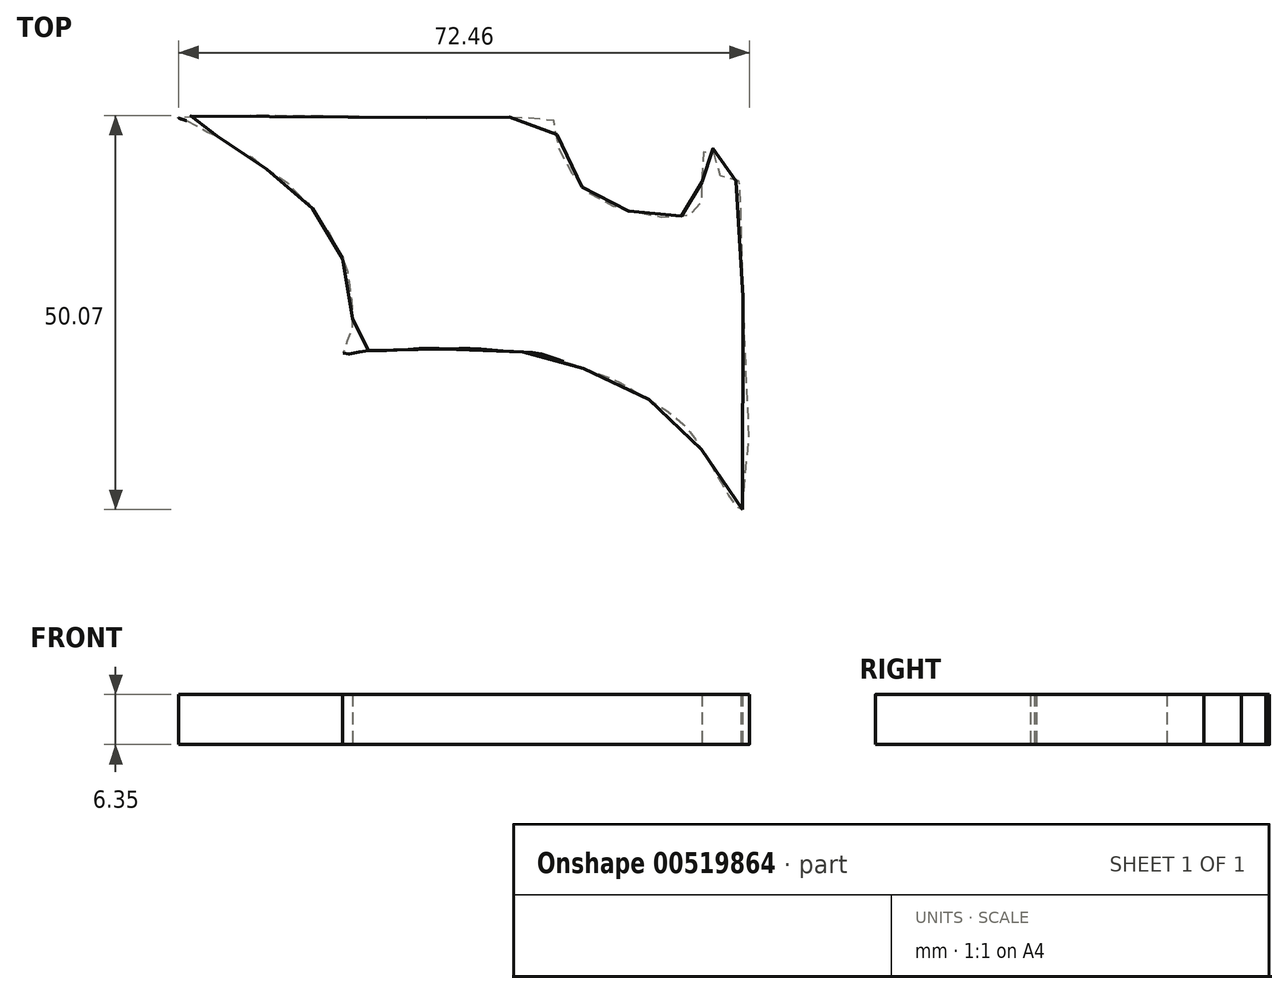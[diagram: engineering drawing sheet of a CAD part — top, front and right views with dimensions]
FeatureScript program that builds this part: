
annotation { "Feature Type Name" : "Feature", "Feature Type Description" : "" }
export const myFeature = defineFeature(function(context is Context, id is Id, definition is map)
    precondition{}
    {
        {
            var Q0;
            Q0=qCreatedBy(makeId("Top.planeOp"),FACE);
            var sketch = newSketch(context, id + "F0", { "sketchPlane" : qUnion([Q0])});
            skFitSpline(sketch, "E0", {"points": [v(0, -28.97) * mm, v(0, 0) * mm, v(0, 12.47) * mm, v(0, 12.69) * mm, v(-1.53, 12.69) * mm, v(-2.51, 12.8) * mm, v(-2.84, 13.67) * mm, v(-3.39, 15.2) * mm, v(-3.72, 16.74) * mm, v(-4.27, 17.5) * mm, v(-4.92, 16.41) * mm, v(-5.14, 14.88) * mm, v(-5.14, 13.45) * mm, v(-5.14, 11.48) * mm, v(-5.25, 9.95) * mm, v(-5.58, 9.29) * mm, v(-6.24, 8.52) * mm, v(-7.88, 8.3) * mm, v(-10.08, 8.08) * mm, v(-11.94, 8.3) * mm, v(-13.25, 8.74) * mm, v(-14.9, 8.96) * mm, v(-16.43, 9.5) * mm, v(-18.3, 10.38) * mm, v(-19.83, 11.48) * mm, v(-20.82, 12.58) * mm, v(-22.24, 14.66) * mm, v(-23.23, 16.63) * mm, v(-23.56, 18.71) * mm, v(-24, 20.47) * mm, v(-25.2, 20.58) * mm, v(-28.05, 20.8) * mm, v(-31.45, 20.8) * mm, v(-35.95, 20.8) * mm, v(-41.65, 20.8) * mm, v(-71.57, 20.8) * mm, v(-70.47, 20.36) * mm, v(-69.27, 19.7) * mm, v(-67.4, 18.71) * mm, v(-65.65, 17.95) * mm, v(-64, 16.63) * mm, v(-62.25, 15.76) * mm, v(-59.95, 13.9) * mm, v(-57.98, 12.69) * mm, v(-56.22, 10.82) * mm, v(-54.69, 9.4) * mm, v(-53.7, 7.53) * mm, v(-52.6, 6.33) * mm, v(-51.51, 4.14) * mm, v(-50.41, 2.05) * mm, v(-49.98, 0) * mm, v(-49.65, -2.55) * mm, v(-49.54, -5.07) * mm, v(-49.87, -6.94) * mm, v(-50.74, -9.13) * mm, v(-48.11, -8.9) * mm, v(-45.37, -8.8) * mm, v(-41.2, -8.58) * mm, v(-37.7, -8.58) * mm, v(-33.75, -8.58) * mm, v(-29.48, -8.9) * mm, v(-26.19, -9.13) * mm, v(-23.89, -9.79) * mm, v(-21.91, -10.44) * mm, v(-19.17, -11.43) * mm, v(-16, -12.64) * mm, v(-13.14, -14.28) * mm, v(-10.08, -16.14) * mm, v(-7.23, -18.45) * mm, v(-5.58, -20.75) * mm, v(-3.5, -24.15) * mm, v(-2.07, -26.67) * mm, v(0, -28.97) * mm]});
            skSolve(sketch);
        }
        {
            var Q0;
            Q0 = qSketchRegion(id + "F0", true);
            var Q1;
            Q1=makeQuery(id+"F0.imprint","IMPRINT",FACE,{"disambiguationData":[TD([[makeQuery(id+"F0.imprint","IMPRINT",EDGE,{"derivedFrom":sQuery(id+"F0.wireOp",EDGE,"E0")}),1.0]])]});
            extrude(context, id + "F1", {"entities" : qUnion([Q0, Q1]), "depth" : 6.35 * mm, "offsetDistance" : 25.4 * mm});
        }
    });
